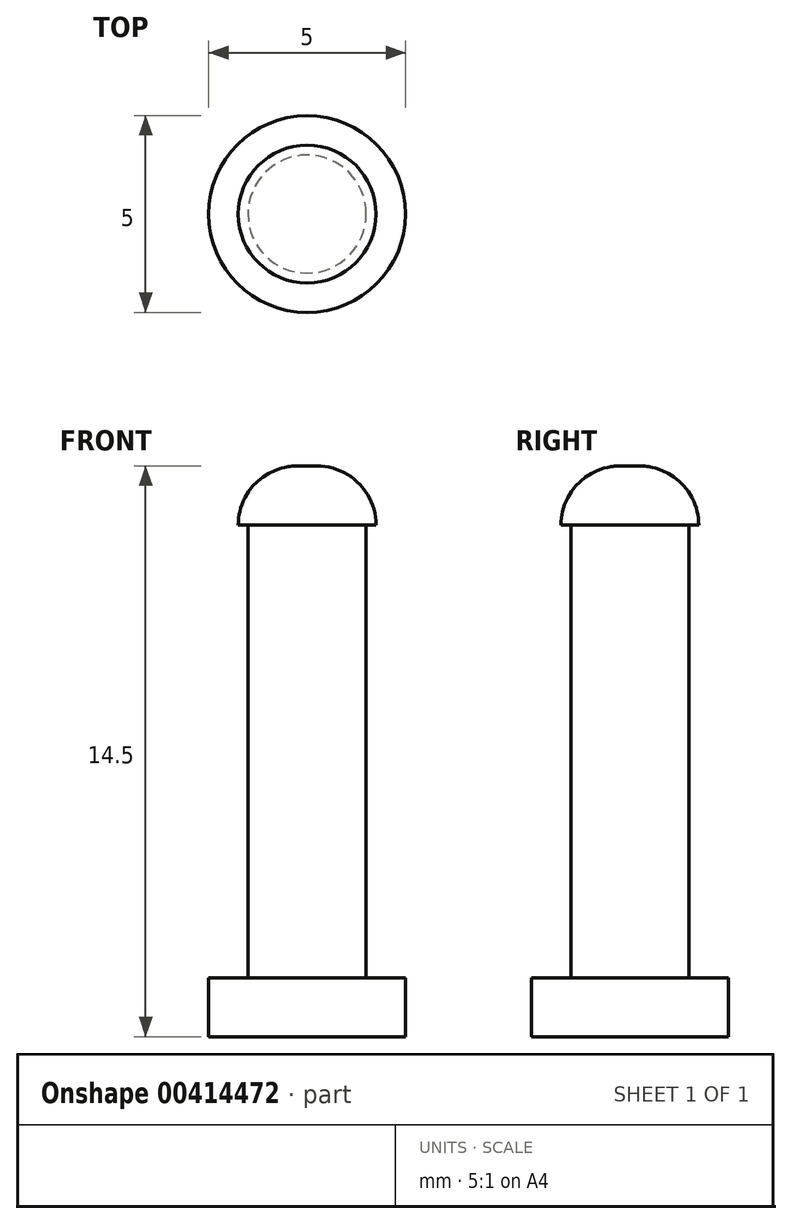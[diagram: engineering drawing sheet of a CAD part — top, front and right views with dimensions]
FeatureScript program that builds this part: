
annotation { "Feature Type Name" : "Feature", "Feature Type Description" : "" }
export const myFeature = defineFeature(function(context is Context, id is Id, definition is map)
    precondition{}
    {
        {
            var Q0;
            Q0=qCreatedBy(makeId("Top.planeOp"),FACE);
            var sketch = newSketch(context, id + "F0", { "sketchPlane" : qUnion([Q0])});
            skCircle(sketch, "E0", {"center": v(0, 0) * mm, "radius": 1.5 * mm});
            skCircle(sketch, "E1", {"center": v(0, 0) * mm, "radius": 2.5 * mm});
            skSolve(sketch);
        }
        {
            var Q0;
            Q0=makeQuery(id+"F0.imprint","IMPRINT",FACE,{"disambiguationData":[TD([[makeQuery(id+"F0.imprint","IMPRINT",EDGE,{"derivedFrom":sQuery(id+"F0.wireOp",EDGE,"E0")}),1.0]])]});
            extrude(context, id + "F1", {"entities" : qUnion([Q0]), "depth" : 13 * mm});
        }
        {
            var Q0;
            Q0 = qSketchRegion(id + "F0", true);
            extrude(context, id + "F2", {"entities" : qUnion([Q0]), "operationType" : NewBodyOperationType.ADD, "depth" : 1.5 * mm});
        }
        {
            var Q0;
            Q0=makeQuery(id+"F1.opExtrude","CAP_FACE",FACE,{"disambiguationData":[OSD([sQuery(id+"F0.wireOp",EDGE,"E0")])],"isStart":false});
            var sketch = newSketch(context, id + "F3", { "sketchPlane" : qUnion([Q0])});
            skCircle(sketch, "E2", {"center": v(0, 0) * mm, "radius": 1.75 * mm});
            skSolve(sketch);
        }
        {
            var Q0;
            Q0 = qSketchRegion(id + "F3", true);
            extrude(context, id + "F4", {"entities" : qUnion([Q0]), "operationType" : NewBodyOperationType.ADD, "depth" : 1.5 * mm});
        }
        {
            var Q0;
            Q0=makeQuery(id+"F4.opExtrude","CAP_EDGE",EDGE,{"disambiguationData":[OSD([sQuery(id+"F3.wireOp",EDGE,"E2")])],"isStart":false});
            fillet(context, id + "F5", {"entities" : qUnion([Q0]), "radius" : 1.5 * mm, "tangentPropagation" : true, "allowEdgeOverflow" : false});
        }
    });
